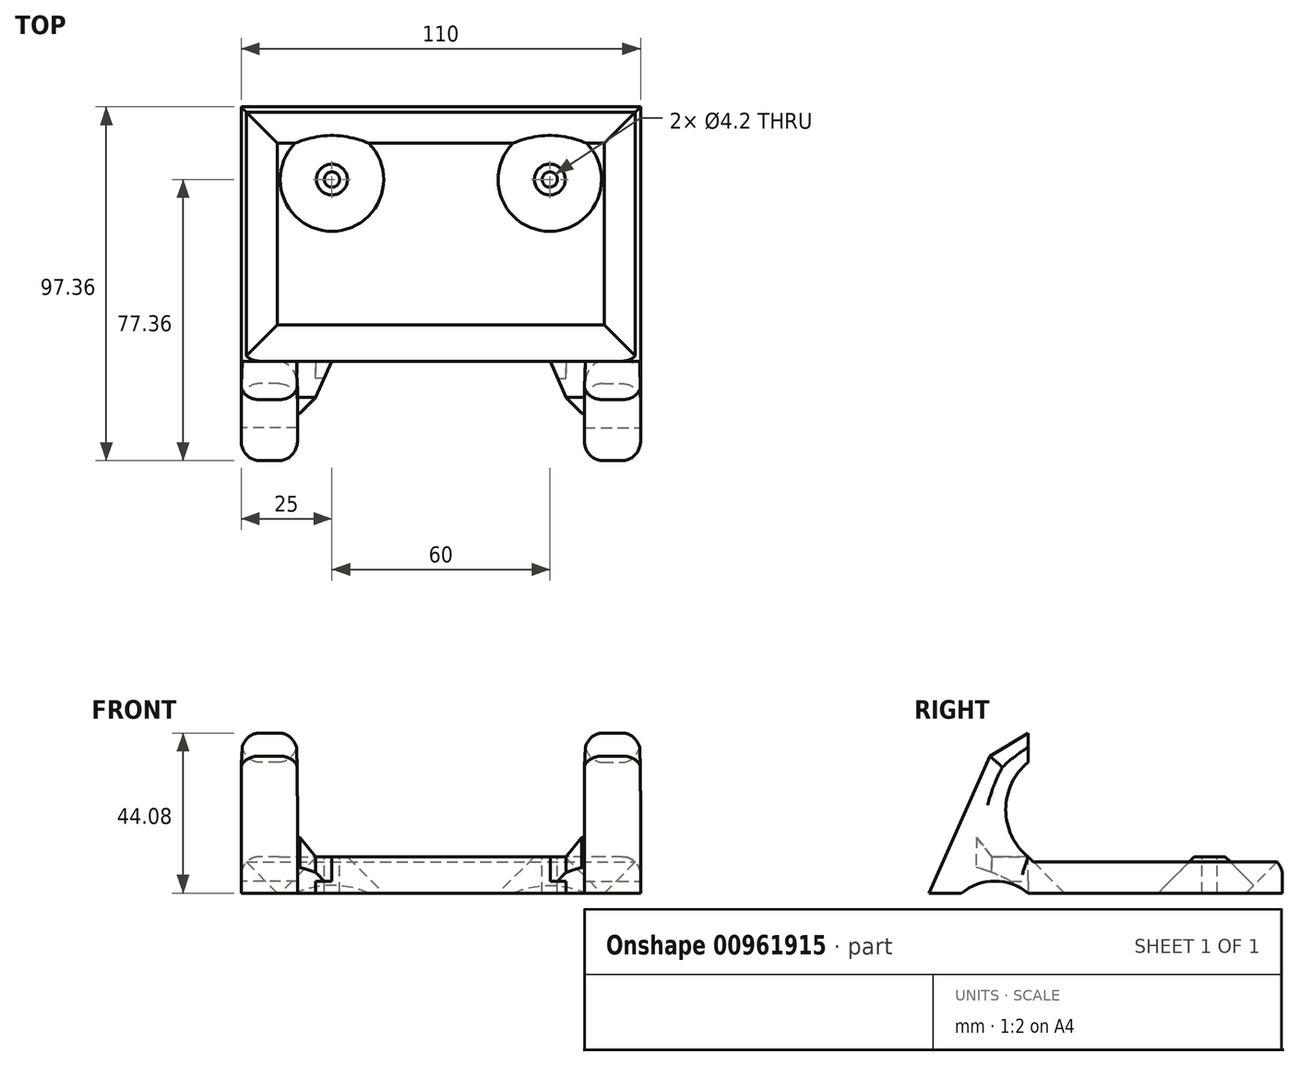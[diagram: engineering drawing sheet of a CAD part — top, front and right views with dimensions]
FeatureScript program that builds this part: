
annotation { "Feature Type Name" : "Feature", "Feature Type Description" : "" }
export const myFeature = defineFeature(function(context is Context, id is Id, definition is map)
    precondition{}
    {
        {
            var Q0;
            Q0=qCreatedBy(makeId("Top.planeOp"),FACE);
            var sketch = newSketch(context, id + "F0", { "sketchPlane" : qUnion([Q0])});
            skLineSegment(sketch, "E0.bottom", {"start": v(55, -35) * mm, "end": v(-55, -35) * mm});
            skLineSegment(sketch, "E0.top", {"start": v(55, 35) * mm, "end": v(-55, 35) * mm});
            skLineSegment(sketch, "E0.left", {"start": v(55, -35) * mm, "end": v(55, 35) * mm});
            skLineSegment(sketch, "E0.right", {"start": v(-55, -35) * mm, "end": v(-55, 35) * mm});
            skPoint(sketch, "E0.middle", {"position": v(0, 0) * mm});
            skSolve(sketch);
        }
        {
            var Q0;
            Q0 = qSketchRegion(id + "F0", true);
            extrude(context, id + "F1", {"entities" : qUnion([Q0]), "depth" : 10 * mm, "offsetDistance" : 25 * mm});
        }
        {
            var Q0;
            Q0=makeQuery(id+"F1.opExtrude","CAP_FACE",FACE,{"disambiguationData":[OSD([sQuery(id+"F0.wireOp",EDGE,"E0.bottom"),sQuery(id+"F0.wireOp",EDGE,"E0.top"),sQuery(id+"F0.wireOp",EDGE,"E0.left"),sQuery(id+"F0.wireOp",EDGE,"E0.right")])],"isStart":false});
            var sketch = newSketch(context, id + "F2", { "sketchPlane" : qUnion([Q0])});
            skLineSegment(sketch, "E1", {"start": v(0, 0) * mm, "end": v(-30, 0) * mm, "construction": true});
            skLineSegment(sketch, "E2", {"start": v(-30, 0) * mm, "end": v(-30, 15) * mm, "construction": true});
            skLineSegment(sketch, "E3", {"start": v(0, 0) * mm, "end": v(0, 35) * mm, "construction": true});
            skCircle(sketch, "E4", {"center": v(-30, 15) * mm, "radius": 4.25 * mm});
            skCircle(sketch, "E5.MirrorC", {"center": v(30, 15) * mm, "radius": 4.25 * mm});
            skCircle(sketch, "E6", {"center": v(-30, 15) * mm, "radius": 2.1 * mm});
            skCircle(sketch, "E7", {"center": v(30, 15) * mm, "radius": 2.1 * mm});
            skSolve(sketch);
        }
        {
            var Q0;
            Q0=makeQuery(id+"F1.opExtrude","SWEPT_FACE",FACE,{"disambiguationData":[OSD([sQuery(id+"F0.wireOp",EDGE,"E0.right")])]});
            var sketch = newSketch(context, id + "F3", { "sketchPlane" : qUnion([Q0])});
            skArc(sketch, "E8", {"start": v(35, 10) * mm, "mid": v(41.17, 23) * mm, "end": v(35, 36) * mm});
            skLineSegment(sketch, "E9", {"start": v(35, 36) * mm, "end": v(35, 44.08) * mm});
            skLineSegment(sketch, "E10", {"start": v(35, 44.08) * mm, "end": v(45.58, 37.73) * mm});
            skLineSegment(sketch, "E11", {"start": v(45.58, 37.73) * mm, "end": v(62.36, 0) * mm});
            skArc(sketch, "E12", {"start": v(53.35, 0) * mm, "mid": v(44.18, 3.27) * mm, "end": v(35, 0) * mm});
            skLineSegment(sketch, "E13", {"start": v(53.35, 0) * mm, "end": v(62.36, 0) * mm});
            skSolve(sketch);
        }
        {
            var Q0;
            Q0 = qSketchRegion(id + "F3", true);
            var Q1;
            Q1=makeQuery(id+"F3.imprint","IMPRINT",FACE,{"disambiguationData":[TD([[makeQuery(id+"F3.imprint","IMPRINT",EDGE,{"derivedFrom":sQuery(id+"F3.wireOp",EDGE,"E8")}),-1.0]])]});
            extrude(context, id + "F4", {"entities" : qUnion([Q0, Q1]), "operationType" : NewBodyOperationType.ADD, "oppositeDirection" : true, "depth" : 15.5 * mm, "offsetDistance" : 25 * mm});
        }
        {
            var Q0;
            Q0=makeQuery(id+"F2.imprint","IMPRINT",FACE,{"disambiguationData":[TD([[makeQuery(id+"F2.imprint","IMPRINT",EDGE,{"derivedFrom":sQuery(id+"F2.wireOp",EDGE,"E4")}),-1.0]])]});
            var sketch = newSketch(context, id + "F5", { "sketchPlane" : qUnion([Q0])});
            skLineSegment(sketch, "E14.0", {"start": v(55, -35) * mm, "end": v(-39.5, -35) * mm});
            skLineSegment(sketch, "E15", {"start": v(-39.5, -35) * mm, "end": v(-39.5, -45) * mm});
            skPoint(sketch, "E16.0", {"position": v(-39.5, -41.17) * mm});
            skLineSegment(sketch, "E17", {"start": v(-39.5, -45) * mm, "end": v(-34.5, -45) * mm});
            skLineSegment(sketch, "E18", {"start": v(-34.5, -45) * mm, "end": v(-30.1, -35) * mm});
            skSolve(sketch);
        }
        {
            var Q0;
            Q0=makeQuery(id+"F4.opExtrude","CAP_FACE",FACE,{"disambiguationData":[OSD([sQuery(id+"F0.wireOp",EDGE,"E0.bottom"),sQuery(id+"F0.wireOp",EDGE,"E0.right"),sQuery(id+"F3.wireOp",EDGE,"E8"),sQuery(id+"F3.wireOp",EDGE,"E9"),sQuery(id+"F3.wireOp",EDGE,"E10"),sQuery(id+"F3.wireOp",EDGE,"E11"),sQuery(id+"F3.wireOp",EDGE,"E12"),sQuery(id+"F3.wireOp",EDGE,"E13")])],"isStart":false});
            var sketch = newSketch(context, id + "F6", { "sketchPlane" : qUnion([Q0])});
            skPoint(sketch, "E19.0", {"position": v(-41.17, 23) * mm});
            skPoint(sketch, "E20.0", {"position": v(-35, 0) * mm});
            skPoint(sketch, "E21.0", {"position": v(-35, 10) * mm});
            skPoint(sketch, "E22.0", {"position": v(-45, 10) * mm});
            skArc(sketch, "E23", {"start": v(-35, 0) * mm, "mid": v(-41.78, 4.3) * mm, "end": v(-49.35, 7.02) * mm});
            skLineSegment(sketch, "E24", {"start": v(-49.35, 7.02) * mm, "end": v(-53.35, 0) * mm});
            skLineSegment(sketch, "E25", {"start": v(-53.35, 0) * mm, "end": v(-35, 0) * mm});
            skLineSegment(sketch, "E26", {"start": v(-35, 5) * mm, "end": v(-35, 0) * mm});
            skLineSegment(sketch, "E27", {"start": v(-45, 10) * mm, "end": v(-49.24, 15.34) * mm});
            skLineSegment(sketch, "E28", {"start": v(-49.24, 15.34) * mm, "end": v(-49.35, 7.02) * mm});
            skLineSegment(sketch, "E29", {"start": v(-45, 10) * mm, "end": v(-35, 10) * mm});
            skSolve(sketch);
        }
        {
            var Q0;
            {var subQ0=sQuery(id+"F5.wireOp",EDGE,"E15");Q0=makeQuery(id+"F5.imprint","IMPRINT",FACE,{"disambiguationData":[TD([[makeQuery(id+"F5.imprint","IMPRINT",EDGE,{"derivedFrom":subQ0}),1.0]])]});}
            extrude(context, id + "F7", {"entities" : qUnion([Q0]), "operationType" : NewBodyOperationType.ADD, "oppositeDirection" : true, "depth" : 6.75 * mm, "offsetDistance" : 25 * mm});
        }
        {
            var Q0;
            {var subQ0=sQuery(id+"F6.wireOp",EDGE,"E26");Q0=makeQuery(id+"F6.imprint","IMPRINT",FACE,{"disambiguationData":[TD([[makeQuery(id+"F6.imprint","IMPRINT",EDGE,{"derivedFrom":subQ0}),-1.0]])]});}
            extrude(context, id + "F8", {"entities" : qUnion([Q0]), "operationType" : NewBodyOperationType.ADD, "depth" : 5 * mm, "offsetDistance" : 25 * mm});
        }
        {
            var Q0;
            {var subQ0=sQuery(id+"F6.wireOp",EDGE,"E24");Q0=makeQuery(id+"F6.imprint","IMPRINT",FACE,{"disambiguationData":[TD([[makeQuery(id+"F6.imprint","IMPRINT",EDGE,{"derivedFrom":subQ0}),1.0]])]});}
            var Q1;
            {var subQ0=sQuery(id+"F6.wireOp",EDGE,"E25");Q1=makeQuery(id+"F6.imprint","IMPRINT",FACE,{"disambiguationData":[TD([[makeQuery(id+"F6.imprint","IMPRINT",EDGE,{"derivedFrom":subQ0}),1.0]])]});}
            extrude(context, id + "F9", {"entities" : qUnion([Q0, Q1]), "operationType" : NewBodyOperationType.REMOVE, "depth" : 25 * mm, "offsetDistance" : 25 * mm});
        }
        {
            var Q0;
            Q0=makeQuery(id+"F1.opExtrude","CAP_EDGE",EDGE,{"disambiguationData":[OSD([sQuery(id+"F0.wireOp",EDGE,"E0.right")])],"isStart":false});
            var Q1;
            Q1=makeQuery(id+"F4.opExtrude","CAP_EDGE",EDGE,{"disambiguationData":[OSD([sQuery(id+"F3.wireOp",EDGE,"E8")])],"isStart":true});
            var Q2;
            Q2=makeQuery(id+"F4.opExtrude","CAP_EDGE",EDGE,{"disambiguationData":[OSD([sQuery(id+"F3.wireOp",EDGE,"E11")])],"isStart":true});
            var Q3;
            Q3=makeQuery(id+"F4.opExtrude","CAP_EDGE",EDGE,{"disambiguationData":[OSD([sQuery(id+"F3.wireOp",EDGE,"E11")])],"isStart":false});
            var Q4;
            Q4=makeQuery(id+"F4.opExtrude","CAP_EDGE",EDGE,{"disambiguationData":[OSD([sQuery(id+"F3.wireOp",EDGE,"E10")])],"isStart":true});
            var Q5;
            Q5=makeQuery(id+"F4.opExtrude","CAP_EDGE",EDGE,{"disambiguationData":[OSD([sQuery(id+"F3.wireOp",EDGE,"E10")])],"isStart":false});
            var Q6;
            Q6=makeQuery(id+"F1.opExtrude","CAP_EDGE",EDGE,{"disambiguationData":[OSD([sQuery(id+"F0.wireOp",EDGE,"E0.top")])],"isStart":false});
            var Q7;
            Q7=makeQuery(id+"F1.opExtrude","CAP_EDGE",EDGE,{"disambiguationData":[OSD([sQuery(id+"F0.wireOp",EDGE,"E0.left")])],"isStart":false});
            var Q8;
            Q8=makeQuery(id+"F4.opExtrude","CAP_EDGE",EDGE,{"disambiguationData":[OSD([sQuery(id+"F3.wireOp",EDGE,"E8")])],"isStart":false});
            fillet(context, id + "F10", {"entities" : qUnion([Q0, Q1, Q2, Q3, Q4, Q5, Q6, Q7, Q8]), "radius" : 5 * mm, "tangentPropagation" : true, "allowEdgeOverflow" : false});
        }
        {
            var Q0;
            Q0=makeQuery(id+"F8.opExtrude","CAP_EDGE",EDGE,{"disambiguationData":[OSD([sQuery(id+"F6.wireOp",EDGE,"E28")])],"isStart":false});
            chamfer(context, id + "F11", {"entities" : qUnion([Q0]), "width" : 4.3 * mm, "tangentPropagation" : true});
        }
        {
            var Q0;
            Q0=makeQuery(id+"F2.imprint","IMPRINT",FACE,{"disambiguationData":[TD([[makeQuery(id+"F2.imprint","IMPRINT",EDGE,{"derivedFrom":sQuery(id+"F2.wireOp",EDGE,"E4")}),1.0]])]});
            var Q1;
            Q1=makeQuery(id+"F2.imprint","IMPRINT",FACE,{"disambiguationData":[TD([[makeQuery(id+"F2.imprint","IMPRINT",EDGE,{"derivedFrom":sQuery(id+"F2.wireOp",EDGE,"E6")}),1.0]])]});
            var Q2;
            Q2=makeQuery(id+"F2.imprint","IMPRINT",FACE,{"disambiguationData":[TD([[makeQuery(id+"F2.imprint","IMPRINT",EDGE,{"derivedFrom":sQuery(id+"F2.wireOp",EDGE,"E5.MirrorC")}),-1.0]])]});
            var Q3;
            Q3=makeQuery(id+"F2.imprint","IMPRINT",FACE,{"disambiguationData":[TD([[makeQuery(id+"F2.imprint","IMPRINT",EDGE,{"derivedFrom":sQuery(id+"F2.wireOp",EDGE,"E7")}),1.0]])]});
            extrude(context, id + "F12", {"entities" : qUnion([Q0, Q1, Q2, Q3]), "operationType" : NewBodyOperationType.REMOVE, "oppositeDirection" : true, "depth" : 25 * mm, "offsetDistance" : 25 * mm, "hasDraft" : true, "draftAngle" : 45 * degree, "draftPullDirection" : true});
        }
        {
            var Q0;
            Q0=makeQuery(id+"F2.imprint","IMPRINT",FACE,{"disambiguationData":[TD([[makeQuery(id+"F2.imprint","IMPRINT",EDGE,{"derivedFrom":sQuery(id+"F2.wireOp",EDGE,"E7")}),1.0]])]});
            var Q1;
            Q1=makeQuery(id+"F2.imprint","IMPRINT",FACE,{"disambiguationData":[TD([[makeQuery(id+"F2.imprint","IMPRINT",EDGE,{"derivedFrom":sQuery(id+"F2.wireOp",EDGE,"E6")}),1.0]])]});
            extrude(context, id + "F13", {"entities" : qUnion([Q0, Q1]), "operationType" : NewBodyOperationType.REMOVE, "oppositeDirection" : true, "depth" : 25 * mm, "offsetDistance" : 25 * mm});
        }
        {
            var Q0;
            Q0=makeQuery(id+"F1.opExtrude","SWEPT_BODY",BODY,{"disambiguationData":[OSD([sQuery(id+"F0.wireOp",EDGE,"E0.bottom"),sQuery(id+"F0.wireOp",EDGE,"E0.top"),sQuery(id+"F0.wireOp",EDGE,"E0.left"),sQuery(id+"F0.wireOp",EDGE,"E0.right")])]});
            var Q1;
            Q1=qCreatedBy(makeId("Right.planeOp"),FACE);
            mirror(context, id + "F14", {"operationType" : NewBodyOperationType.ADD, "entities" : qUnion([Q0]), "mirrorPlane" : qUnion([Q1])});
        }
        {
            var Q0;
            Q0=makeQuery(id+"F2.imprint","IMPRINT",FACE,{"disambiguationData":[TD([[makeQuery(id+"F2.imprint","IMPRINT",EDGE,{"derivedFrom":sQuery(id+"F2.wireOp",EDGE,"E4")}),-1.0]])]});
            var sketch = newSketch(context, id + "F15", { "sketchPlane" : qUnion([Q0])});
            skText(sketch, "E30", { "text": "CSULB", "fontName": "AllertaStencil-Regular.ttf"});
            const initialGuessF15  = {"E30": [-0.025, -0.01607, 1, 0, 0.01153]};
            skSetInitialGuess(sketch, initialGuessF15);
            skSolve(sketch);
        }
        {
            var Q0;
            Q0 = qSketchRegion(id + "F15", true);
            extrude(context, id + "F16", {"entities" : qUnion([Q0]), "operationType" : NewBodyOperationType.REMOVE, "oppositeDirection" : true, "depth" : 1.5 * mm, "offsetDistance" : 25 * mm});
        }
    });
